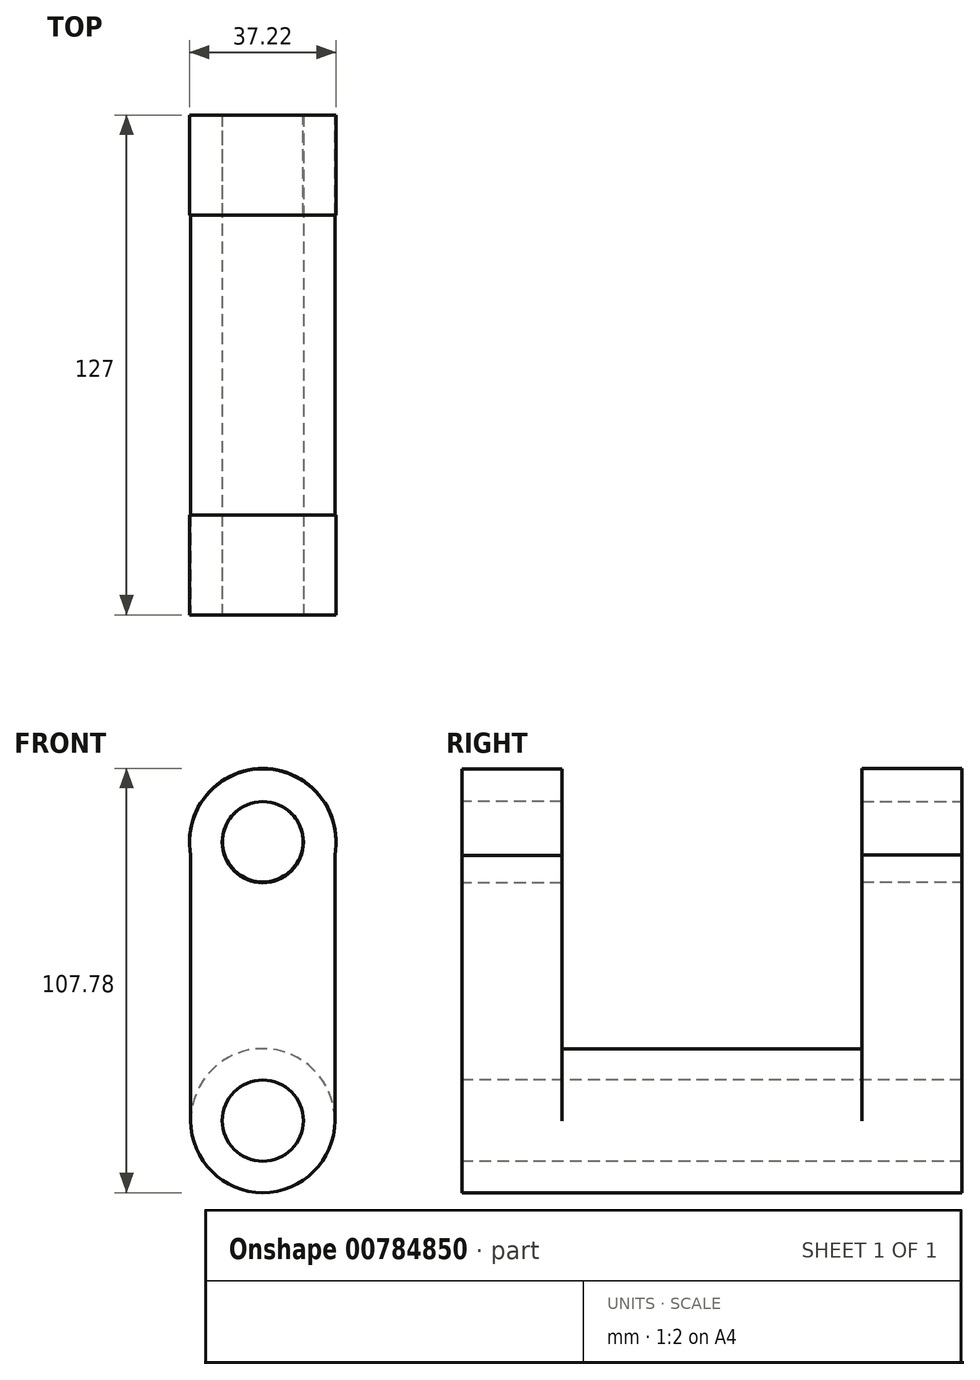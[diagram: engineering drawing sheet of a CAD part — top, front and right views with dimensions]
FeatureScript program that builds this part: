
annotation { "Feature Type Name" : "Feature", "Feature Type Description" : "" }
export const myFeature = defineFeature(function(context is Context, id is Id, definition is map)
    precondition{}
    {
        {
            var Q0;
            Q0=qCreatedBy(makeId("Front.planeOp"),FACE);
            var sketch = newSketch(context, id + "F0", { "sketchPlane" : qUnion([Q0])});
            skCircle(sketch, "E0", {"center": v(0, 0) * mm, "radius": 18.3 * mm});
            skCircle(sketch, "E1", {"center": v(0, 0) * mm, "radius": 10.32 * mm});
            skLineSegment(sketch, "E2", {"start": v(-18.3, 0) * mm, "end": v(-18.3, 67.36) * mm});
            skLineSegment(sketch, "E3", {"start": v(18.3, 0) * mm, "end": v(18.3, 67.36) * mm});
            skArc(sketch, "E4", {"start": v(18.3, 67.36) * mm, "mid": v(0, 89.36) * mm, "end": v(-18.3, 67.36) * mm});
            skCircle(sketch, "E5", {"center": v(0, 70.75) * mm, "radius": 10.32 * mm});
            skSolve(sketch);
        }
        {
            var Q0;
            Q0=makeQuery(id+"F0.imprint","IMPRINT",FACE,{"disambiguationData":[TD([[makeQuery(id+"F0.imprint","IMPRINT",EDGE,{"derivedFrom":sQuery(id+"F0.wireOp",EDGE,"E1")}),-1.0]])]});
            extrude(context, id + "F1", {"entities" : qUnion([Q0]), "oppositeDirection" : true, "depth" : 127 * mm, "offsetDistance" : 25.4 * mm});
        }
        {
            var Q0;
            Q0 = qSketchRegion(id + "F0", true);
            extrude(context, id + "F2", {"entities" : qUnion([Q0]), "operationType" : NewBodyOperationType.ADD, "oppositeDirection" : true, "depth" : 25.4 * mm, "offsetDistance" : 25.4 * mm});
        }
        {
            var Q0;
            Q0=makeQuery(id+"F1.opExtrude","CAP_FACE",FACE,{"disambiguationData":[OSD([sQuery(id+"F0.wireOp",EDGE,"E0"),sQuery(id+"F0.wireOp",EDGE,"E1")])],"isStart":false});
            var sketch = newSketch(context, id + "F3", { "sketchPlane" : qUnion([Q0])});
            skLineSegment(sketch, "E6", {"start": v(-18.3, 0) * mm, "end": v(-18.3, 67.45) * mm});
            skLineSegment(sketch, "E7", {"start": v(18.3, 0) * mm, "end": v(18.3, 67.45) * mm});
            skArc(sketch, "E8", {"start": v(18.3, 67.45) * mm, "mid": v(0, 89.5) * mm, "end": v(-18.3, 67.45) * mm});
            skCircle(sketch, "E9", {"center": v(0, 70.88) * mm, "radius": 10.22 * mm});
            skSolve(sketch);
        }
        {
            var Q0;
            {var subQ1=sQuery(id+"F3.wireOp",EDGE,"E6");Q0=makeQuery(id+"F3.imprint","IMPRINT",FACE,{"disambiguationData":[TD([[makeQuery(id+"F3.imprint","IMPRINT",EDGE,{"derivedFrom":subQ1}),-1.0]])]});}
            extrude(context, id + "F4", {"entities" : qUnion([Q0]), "operationType" : NewBodyOperationType.ADD, "oppositeDirection" : true, "depth" : 25.4 * mm, "offsetDistance" : 25.4 * mm});
        }
    });
